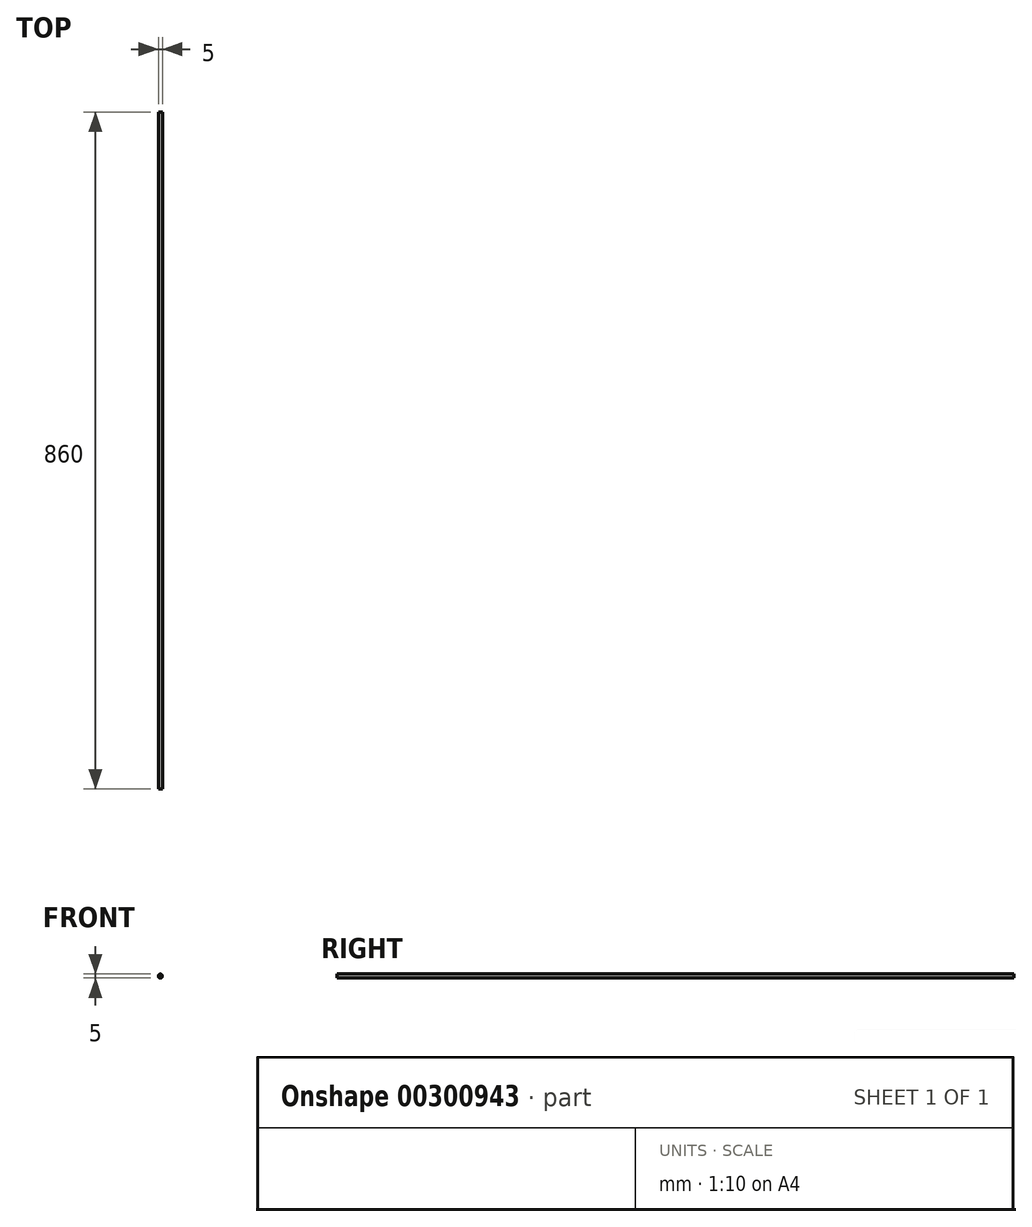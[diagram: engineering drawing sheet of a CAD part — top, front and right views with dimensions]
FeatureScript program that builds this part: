
annotation { "Feature Type Name" : "Feature", "Feature Type Description" : "" }
export const myFeature = defineFeature(function(context is Context, id is Id, definition is map)
    precondition{}
    {
        {
            var Q0;
            Q0=qCreatedBy(makeId("Front.planeOp"),FACE);
            var sketch = newSketch(context, id + "F0", { "sketchPlane" : qUnion([Q0])});
            skCircle(sketch, "E0", {"center": v(0, 0) * mm, "radius": 2.5 * mm});
            skSolve(sketch);
        }
        {
            var Q0;
            Q0=makeQuery(id+"F0.imprint","IMPRINT",FACE,{"disambiguationData":[TD([[makeQuery(id+"F0.imprint","IMPRINT",EDGE,{"derivedFrom":sQuery(id+"F0.wireOp",EDGE,"E0")}),1.0]])]});
            extrude(context, id + "F1", {"entities" : qUnion([Q0]), "depth" : 860 * mm});
        }
    });
